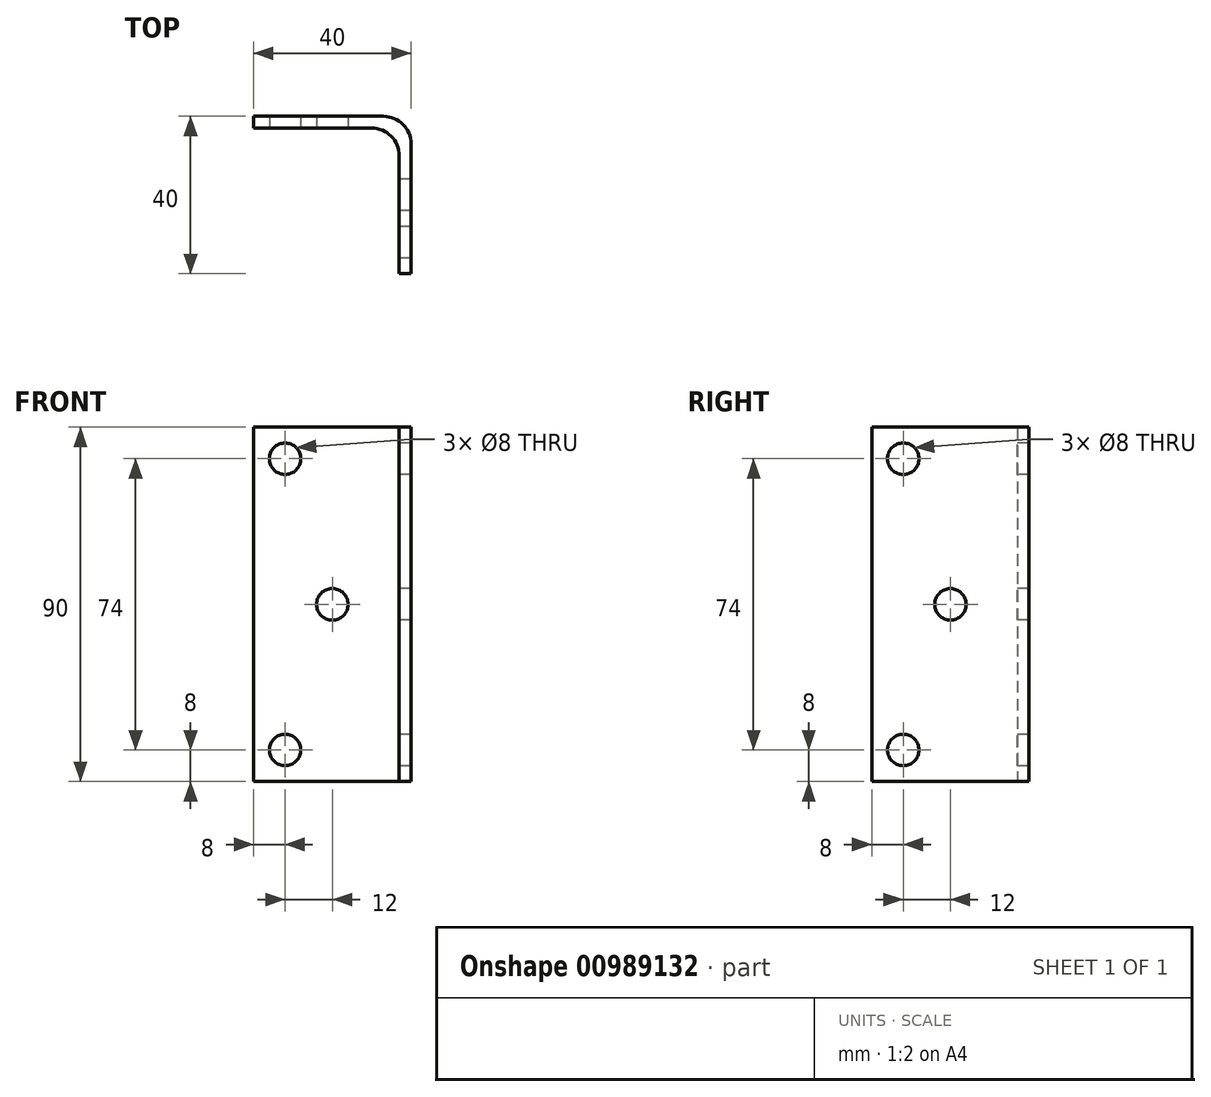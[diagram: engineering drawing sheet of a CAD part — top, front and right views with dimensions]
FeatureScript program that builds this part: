
annotation { "Feature Type Name" : "Feature", "Feature Type Description" : "" }
export const myFeature = defineFeature(function(context is Context, id is Id, definition is map)
    precondition{}
    {
        {
            var Q0;
            Q0=qCreatedBy(makeId("Top.planeOp"),FACE);
            var sketch = newSketch(context, id + "F0", { "sketchPlane" : qUnion([Q0])});
            skLineSegment(sketch, "E0", {"start": v(0, 0) * mm, "end": v(-40, 0) * mm});
            skLineSegment(sketch, "E1", {"start": v(0, 0) * mm, "end": v(0, -40) * mm});
            skLineSegment(sketch, "E2.0", {"start": v(-3, -3) * mm, "end": v(-3, -40) * mm});
            skLineSegment(sketch, "E2.1", {"start": v(-3, -3) * mm, "end": v(-40, -3) * mm});
            skLineSegment(sketch, "E3", {"start": v(-3, -40) * mm, "end": v(0, -40) * mm});
            skLineSegment(sketch, "E4", {"start": v(-40, -3) * mm, "end": v(-40, 0) * mm});
            skSolve(sketch);
        }
        {
            var Q0;
            Q0 = qSketchRegion(id + "F0", true);
            extrude(context, id + "F1", {"entities" : qUnion([Q0]), "endBound" : BoundingType.SYMMETRIC, "depth" : 90 * mm, "offsetDistance" : 25 * mm});
        }
        {
            var Q0;
            Q0=makeQuery(id+"F1.opExtrude","SWEPT_EDGE",EDGE,{"disambiguationData":[OSD([sQuery(id+"F0.wireOp",EDGE,"E2.0"),sQuery(id+"F0.wireOp",EDGE,"E2.1")])]});
            var Q1;
            Q1=makeQuery(id+"F1.opExtrude","SWEPT_EDGE",EDGE,{"disambiguationData":[OSD([sQuery(id+"F0.wireOp",EDGE,"E0"),sQuery(id+"F0.wireOp",EDGE,"E1")])]});
            fillet(context, id + "F2", {"entities" : qUnion([Q0, Q1]), "radius" : 7 * mm, "tangentPropagation" : true, "allowEdgeOverflow" : false});
        }
        {
            var Q0;
            Q0=makeQuery(id+"F1.opExtrude","SWEPT_FACE",FACE,{"disambiguationData":[OSD([sQuery(id+"F0.wireOp",EDGE,"E2.1")])]});
            var sketch = newSketch(context, id + "F3", { "sketchPlane" : qUnion([Q0])});
            skLineSegment(sketch, "E5", {"start": v(-40, 0) * mm, "end": v(0, 0) * mm, "construction": true});
            skCircle(sketch, "E6", {"center": v(-32, 37) * mm, "radius": 4 * mm});
            skCircle(sketch, "E7", {"center": v(-20, 0) * mm, "radius": 4 * mm});
            skCircle(sketch, "E8", {"center": v(-32, -37) * mm, "radius": 4 * mm});
            skSolve(sketch);
        }
        {
            var Q0;
            Q0 = qSketchRegion(id + "F3", true);
            extrude(context, id + "F4", {"entities" : qUnion([Q0]), "operationType" : NewBodyOperationType.REMOVE, "endBound" : BoundingType.THROUGH_ALL, "oppositeDirection" : true, "depth" : 25 * mm, "offsetDistance" : 25 * mm});
        }
        {
            var Q0;
            Q0=makeQuery(id+"F1.opExtrude","SWEPT_FACE",FACE,{"disambiguationData":[OSD([sQuery(id+"F0.wireOp",EDGE,"E2.0")])]});
            var sketch = newSketch(context, id + "F5", { "sketchPlane" : qUnion([Q0])});
            skLineSegment(sketch, "E9", {"start": v(40, 0) * mm, "end": v(0, 0) * mm, "construction": true});
            skCircle(sketch, "E10", {"center": v(32, 37) * mm, "radius": 4 * mm});
            skCircle(sketch, "E11", {"center": v(20, 0) * mm, "radius": 4 * mm});
            skCircle(sketch, "E12", {"center": v(32, -37) * mm, "radius": 4 * mm});
            skSolve(sketch);
        }
        {
            var Q0;
            Q0 = qSketchRegion(id + "F5", true);
            extrude(context, id + "F6", {"entities" : qUnion([Q0]), "operationType" : NewBodyOperationType.REMOVE, "endBound" : BoundingType.THROUGH_ALL, "oppositeDirection" : true, "depth" : 25 * mm, "offsetDistance" : 25 * mm});
        }
    });
